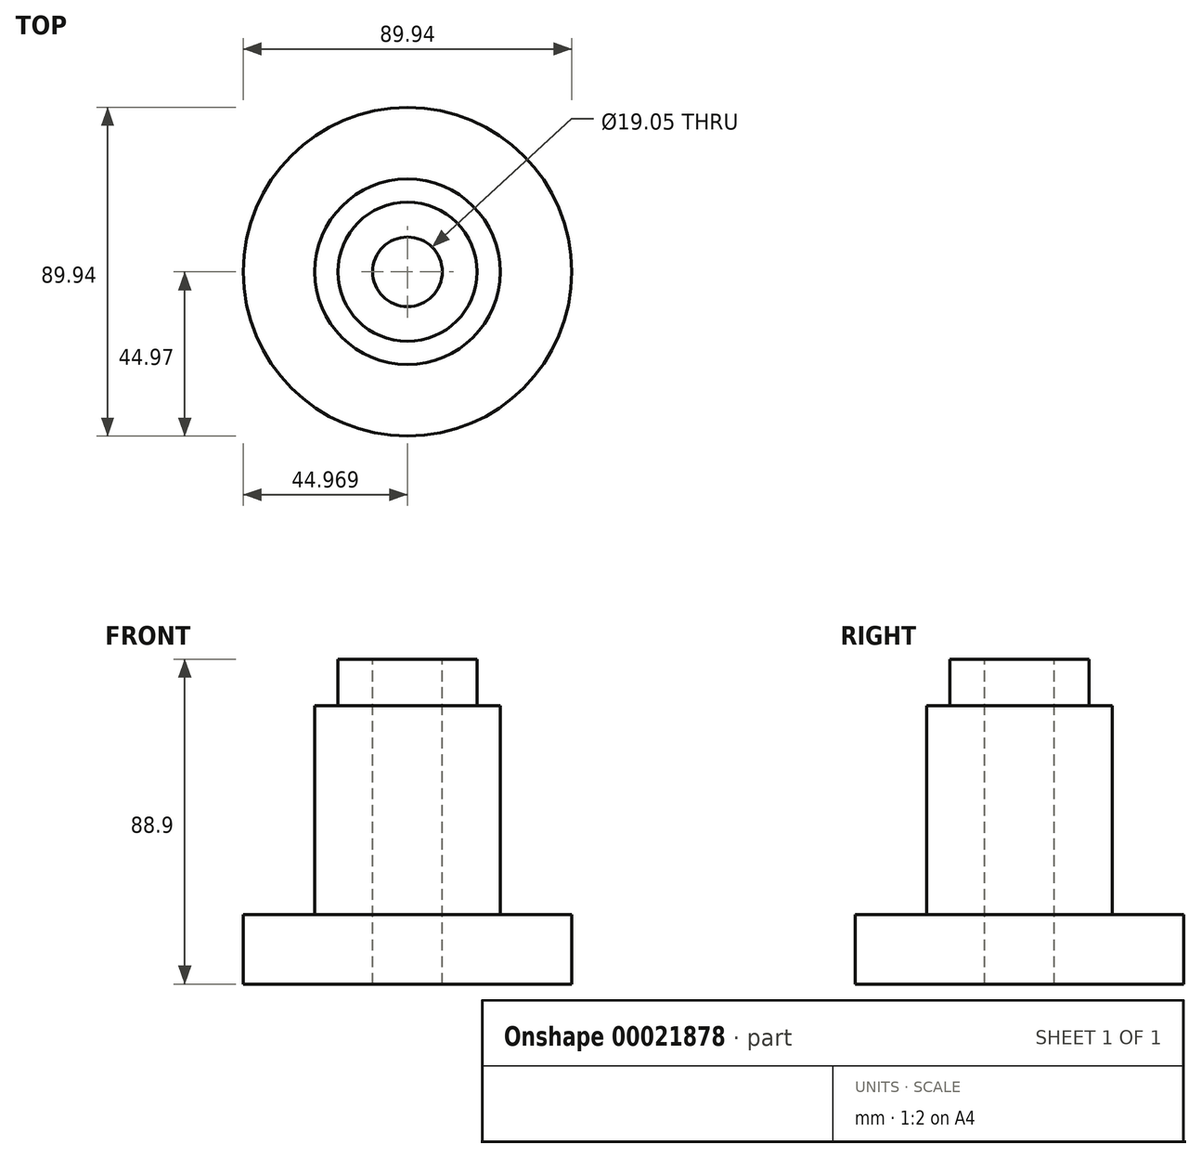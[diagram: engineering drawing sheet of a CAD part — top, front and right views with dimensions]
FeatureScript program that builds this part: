
annotation { "Feature Type Name" : "Feature", "Feature Type Description" : "" }
export const myFeature = defineFeature(function(context is Context, id is Id, definition is map)
    precondition{}
    {
        {
            var Q0;
            Q0=qCreatedBy(makeId("Front.planeOp"),FACE);
            var sketch = newSketch(context, id + "F0", { "sketchPlane" : qUnion([Q0])});
            skLineSegment(sketch, "E0", {"start": v(5.85, -50.62) * mm, "end": v(5.85, -63.32) * mm});
            skLineSegment(sketch, "E1", {"start": v(12.2, -63.32) * mm, "end": v(12.2, -120.47) * mm});
            skLineSegment(sketch, "E2", {"start": v(31.77, -120.47) * mm, "end": v(31.77, -139.52) * mm});
            skLineSegment(sketch, "E3", {"start": v(-13.2, -50.62) * mm, "end": v(-13.2, -120.47) * mm});
            skLineSegment(sketch, "E4", {"start": v(-13.2, -120.47) * mm, "end": v(-13.2, -120.47) * mm});
            skLineSegment(sketch, "E5", {"start": v(-13.2, -72.77) * mm, "end": v(-13.2, -120.47) * mm});
            skLineSegment(sketch, "E6", {"start": v(-3.68, -139.52) * mm, "end": v(31.77, -139.52) * mm});
            skLineSegment(sketch, "E7", {"start": v(-13.2, -72.77) * mm, "end": v(-13.2, -139.52) * mm});
            skLineSegment(sketch, "E8", {"start": v(12.2, -63.32) * mm, "end": v(5.85, -63.32) * mm});
            skLineSegment(sketch, "E9", {"start": v(-3.68, -50.62) * mm, "end": v(-3.68, -139.52) * mm});
            skLineSegment(sketch, "E10", {"start": v(-3.68, -50.62) * mm, "end": v(5.85, -50.62) * mm});
            skLineSegment(sketch, "E11", {"start": v(12.2, -120.47) * mm, "end": v(31.77, -120.47) * mm});
            skSolve(sketch);
        }
        {
            var Q0;
            Q0=makeQuery(id+"F0.imprint","IMPRINT",FACE,{"disambiguationData":[TD([[makeQuery(id+"F0.imprint","IMPRINT",EDGE,{"derivedFrom":sQuery(id+"F0.wireOp",EDGE,"E0")}),-1.0]])]});
            var Q1;
            Q1=sQuery(id+"F0.wireOp",EDGE,"E3");
            revolve(context, id + "F1", {"entities" : qUnion([Q0]), "axis" : qUnion([Q1]), "revolveType" : RevolveType.FULL});
        }
    });
